# Revit family: CFP
name_source: partatom
category: Lighting Fixtures
revit_build: Autodesk Revit 2013 (Build: 20130531_2115(x64)
units: mm (PartAtom-declared; Revit-internal decimal feet)

## types (4) — shared parameters
Assembly Code = D5020200
Color Filter = 16777215
Default Elevation = 4' - 0"
Description = Edge-lit Flat Panel
Dimming Lamp Color Temperature Shift = <None>
Emit Shape Visible in Rendering = No
Emit from Rectangle Width = 1' - 9 7/8"
Lamp = LED Lamp
Load Classification = Lighting
Manufacturer = Columbia Lighting
Manufacturer Fax = 866-898-1065
Material Finish = Paint  - Hubbell - White
Model = CFP
Mounting Type = Recessed mount
Opal lens = Hubbell - White Glass
Power Factor = 1
Technical Support = 864-678-1000
Tilt Angle = -90.00°
URL = http://www.columbialighting.com
Voltage = 120 V
Warranty = Five year warranty
Wattage Comments = 31.7W to 40.1W
zz Length 2 = 1' - 11 7/8"

## per-type parameters (varying)
| type | Apparent Load | Emit from Rectangle Length | Photometric Web File | Watts | zz Length 1 |
| CFP24-4135 | 40 VA | 3' - 9 7/8" | CFP24-4135.ies | 40 W | 3' - 11 7/8" |
| CFP24-4140 | 40 VA | 3' - 9 7/8" | CFP24-4140.ies | 40 W | 3' - 11 7/8" |
| CFP22-3335 | 32 VA | 1' - 9 7/8" | CFP22-3335.ies | 32 W | 1' - 11 7/8" |
| CFP22-3340 | 32 VA | 1' - 9 7/8" | CFP22-3340.ies | 32 W | 1' - 11 7/8" |

## geometry (parser evidence)
native form markers: Sweep x1
no freeform markers — native parametric forms only
